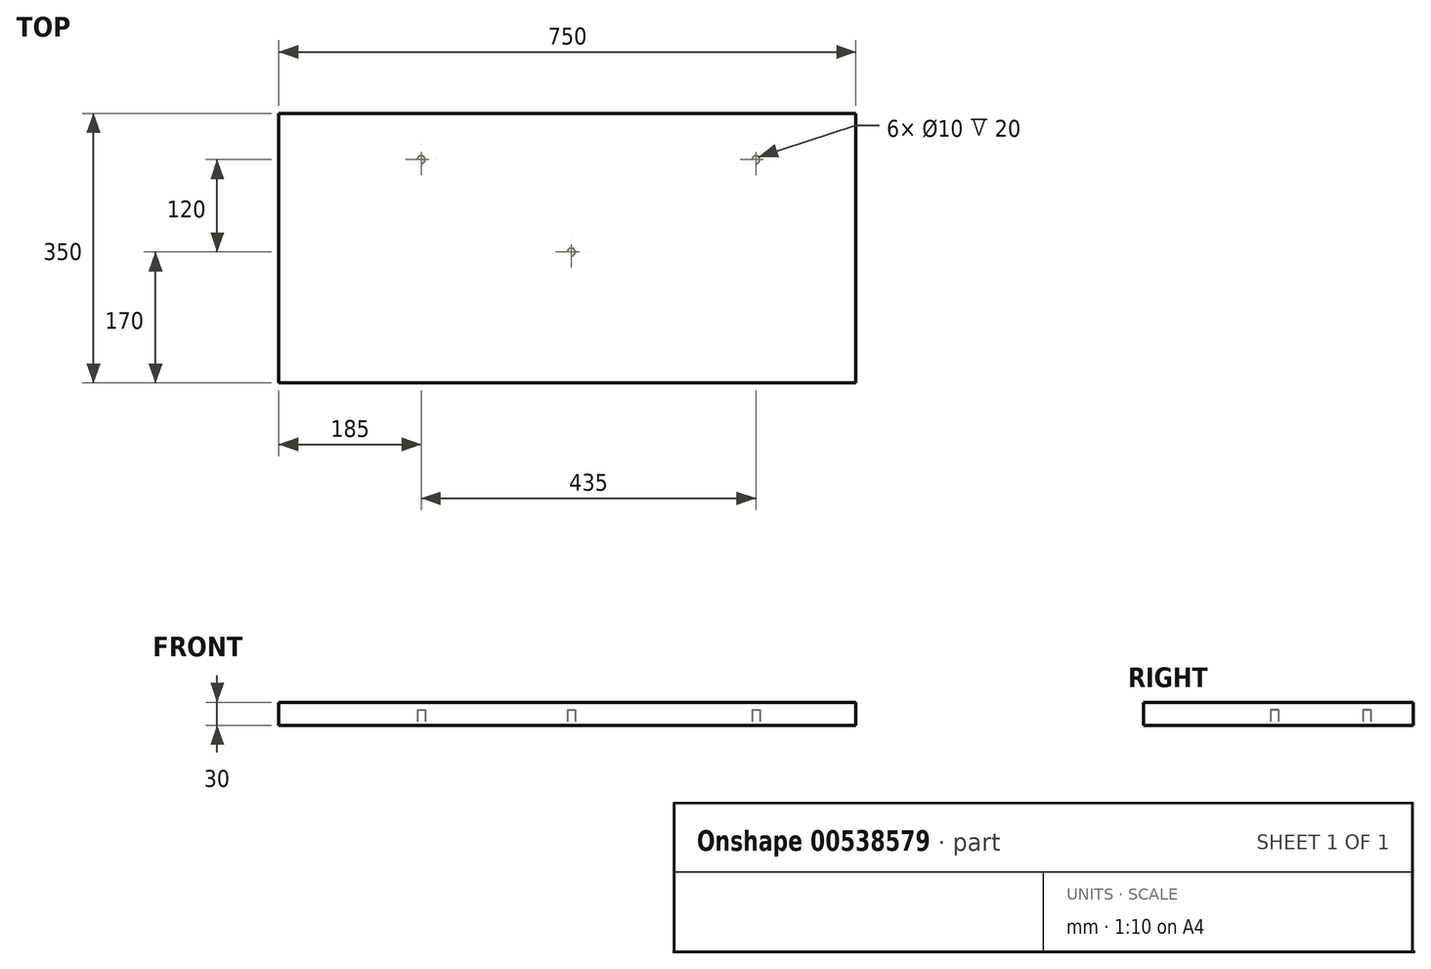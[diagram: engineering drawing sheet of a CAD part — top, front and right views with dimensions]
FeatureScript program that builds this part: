
annotation { "Feature Type Name" : "Feature", "Feature Type Description" : "" }
export const myFeature = defineFeature(function(context is Context, id is Id, definition is map)
    precondition{}
    {
        {
            var Q0;
            Q0=qCreatedBy(makeId("Top.planeOp"),FACE);
            var sketch = newSketch(context, id + "F0", { "sketchPlane" : qUnion([Q0])});
            skLineSegment(sketch, "E0.bottom", {"start": v(0, 0) * mm, "end": v(750, 0) * mm});
            skLineSegment(sketch, "E0.top", {"start": v(0, 350) * mm, "end": v(750, 350) * mm});
            skLineSegment(sketch, "E0.left", {"start": v(0, 0) * mm, "end": v(0, 350) * mm});
            skLineSegment(sketch, "E0.right", {"start": v(750, 0) * mm, "end": v(750, 350) * mm});
            skSolve(sketch);
        }
        {
            var Q0;
            Q0=makeQuery(id+"F0.imprint","IMPRINT",FACE,{"disambiguationData":[TD([[makeQuery(id+"F0.imprint","IMPRINT",EDGE,{"derivedFrom":sQuery(id+"F0.wireOp",EDGE,"E0.bottom")}),1.0]])]});
            extrude(context, id + "F1", {"entities" : qUnion([Q0]), "depth" : 30 * mm, "offsetDistance" : 25 * mm});
        }
        {
            var Q0;
            Q0=makeQuery(id+"F1.opExtrude","CAP_FACE",FACE,{"disambiguationData":[OSD([sQuery(id+"F0.wireOp",EDGE,"E0.bottom"),sQuery(id+"F0.wireOp",EDGE,"E0.top"),sQuery(id+"F0.wireOp",EDGE,"E0.left"),sQuery(id+"F0.wireOp",EDGE,"E0.right")])],"isStart":true});
            var sketch = newSketch(context, id + "F2", { "sketchPlane" : qUnion([Q0])});
            skCircle(sketch, "E1", {"center": v(380, -170) * mm, "radius": 5 * mm});
            skSolve(sketch);
        }
        {
            var Q0;
            Q0 = qSketchRegion(id + "F2", true);
            extrude(context, id + "F3", {"entities" : qUnion([Q0]), "operationType" : NewBodyOperationType.REMOVE, "oppositeDirection" : true, "depth" : 20 * mm, "offsetDistance" : 25 * mm});
        }
        {
            var Q0;
            Q0=makeQuery(id+"F1.opExtrude","CAP_FACE",FACE,{"disambiguationData":[OSD([sQuery(id+"F0.wireOp",EDGE,"E0.bottom"),sQuery(id+"F0.wireOp",EDGE,"E0.top"),sQuery(id+"F0.wireOp",EDGE,"E0.left"),sQuery(id+"F0.wireOp",EDGE,"E0.right")])],"isStart":true});
            var sketch = newSketch(context, id + "F4", { "sketchPlane" : qUnion([Q0])});
            skCircle(sketch, "E2", {"center": v(620, -290) * mm, "radius": 5 * mm});
            skSolve(sketch);
        }
        {
            var Q0;
            Q0 = qSketchRegion(id + "F4", true);
            extrude(context, id + "F5", {"entities" : qUnion([Q0]), "operationType" : NewBodyOperationType.REMOVE, "oppositeDirection" : true, "depth" : 20 * mm, "offsetDistance" : 25 * mm});
        }
        {
            var Q0;
            Q0=makeQuery(id+"F1.opExtrude","CAP_FACE",FACE,{"disambiguationData":[OSD([sQuery(id+"F0.wireOp",EDGE,"E0.bottom"),sQuery(id+"F0.wireOp",EDGE,"E0.top"),sQuery(id+"F0.wireOp",EDGE,"E0.left"),sQuery(id+"F0.wireOp",EDGE,"E0.right")])],"isStart":true});
            var sketch = newSketch(context, id + "F6", { "sketchPlane" : qUnion([Q0])});
            skCircle(sketch, "E3", {"center": v(185, -290) * mm, "radius": 5 * mm});
            skSolve(sketch);
        }
        {
            var Q0;
            Q0 = qSketchRegion(id + "F6", true);
            extrude(context, id + "F7", {"entities" : qUnion([Q0]), "operationType" : NewBodyOperationType.REMOVE, "oppositeDirection" : true, "depth" : 20 * mm, "offsetDistance" : 25 * mm});
        }
    });
